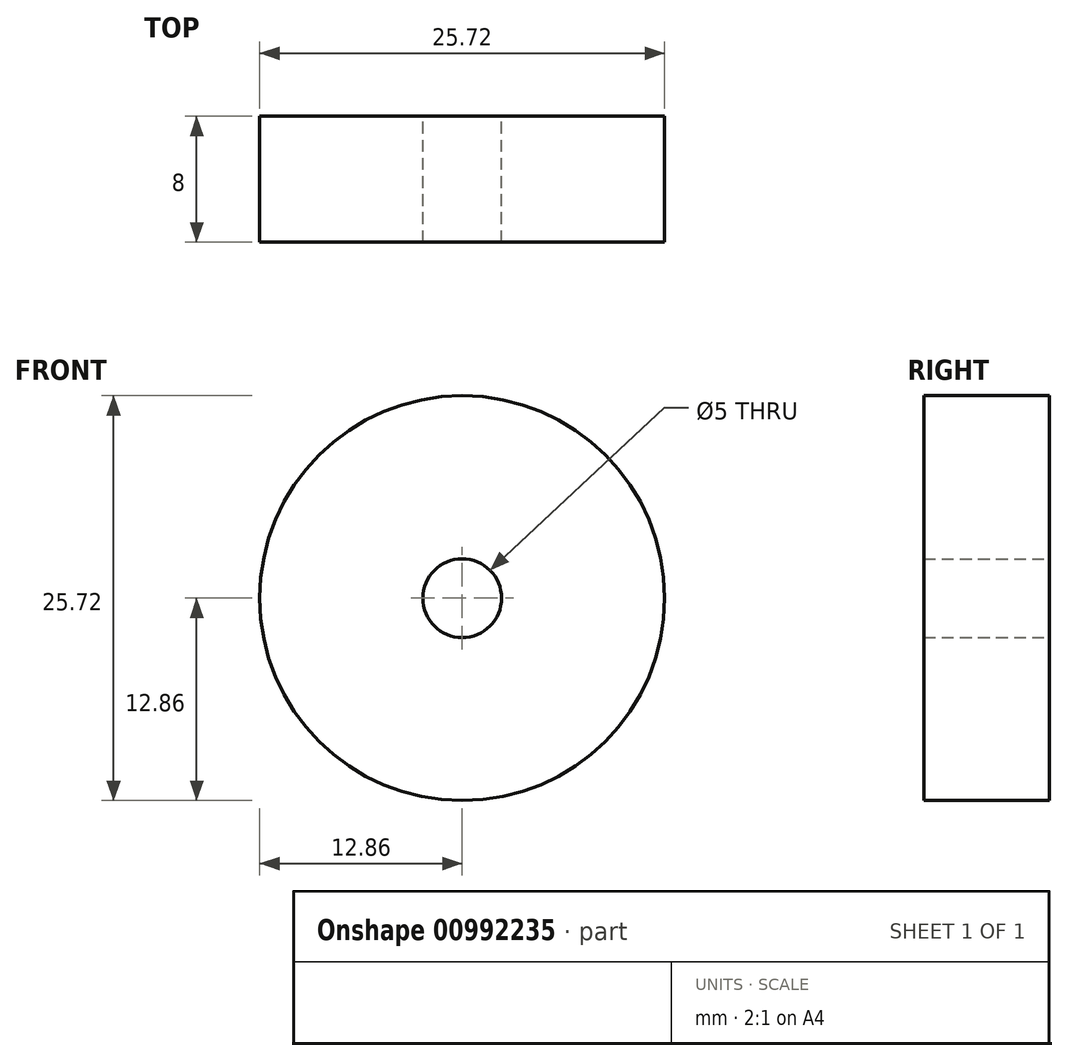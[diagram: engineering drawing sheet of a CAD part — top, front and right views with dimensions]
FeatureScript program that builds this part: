
annotation { "Feature Type Name" : "Feature", "Feature Type Description" : "" }
export const myFeature = defineFeature(function(context is Context, id is Id, definition is map)
    precondition{}
    {
        {
            var Q0;
            Q0=qCreatedBy(makeId("Front.planeOp"),FACE);
            var sketch = newSketch(context, id + "F0", { "sketchPlane" : qUnion([Q0])});
            skCircle(sketch, "E0", {"center": v(0, 0) * mm, "radius": 12.86 * mm});
            skCircle(sketch, "E1", {"center": v(0, 0) * mm, "radius": 2.5 * mm});
            skSolve(sketch);
        }
        {
            var Q0;
            Q0=makeQuery(id+"F0.imprint","IMPRINT",FACE,{"disambiguationData":[TD([[makeQuery(id+"F0.imprint","IMPRINT",EDGE,{"derivedFrom":sQuery(id+"F0.wireOp",EDGE,"E0")}),1.0]])]});
            extrude(context, id + "F1", {"entities" : qUnion([Q0]), "endBound" : BoundingType.SYMMETRIC, "depth" : 8 * mm, "offsetDistance" : 25 * mm});
        }
    });
